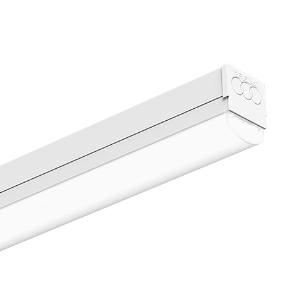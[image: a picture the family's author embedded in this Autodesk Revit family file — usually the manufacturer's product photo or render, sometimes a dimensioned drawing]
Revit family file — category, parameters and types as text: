
# Revit family: 3f_filippi_-_3f_zeta_d_3f_filippi_-_10870_-_3f_zeta_d_1x22_led_l1489
name_source: partatom
category: Lighting Fixtures
units: mm (PartAtom-declared; Revit-internal decimal feet)

## family parameters
Cut with Voids When Loaded = No
Host = Face
Light Source = No
Part Type = Normal
Room Calculation Point = No
Round Connector Dimension = Use Diameter
Shared = No

## types (1)
- 3F Filippi - 3F Zeta D (1 x LED, 3118 lm, 24.5 W, 4000 K)
    Apparent Load = 25 VA
    Approval mark = CE
    CIE Flux Codes = 42 71 90 91 100
    Color Rendering = 80
    Color Temperature = 4000 K
    Control Gear = Electronic ballast
    Default Elevation = 1800 mm
    Description = ILLUMINOTECHNICAL
Luminous efficiency 100% (DLOR 91%, ULOR 9%).
Initial luminous flux of the luminaire 3118 lm.
Diffused symmetric distribution.
Installation Interdistance Transv.D = 1.31 x hu - Long.D = 1.25 x hu.
Tabular UGR (CIE 117 - 4H-8H; S=0.25H; 70/50/20): RUG 23.8 - 22.2.
Beam angle: 130° - 112°.
Luminous efficacy 127 lm/W.
Lifetime (L93/B10): 30000 h. (tq+25°C)
Lifetime (L90/B10): 50000 h. (tq+25°C)
Lifetime (L85/B10): 80000 h. (tq+25°C)
Lifetime (L80/B10): 100000 h. (tq+25°C)
Sudden decreased luminous flux after 50000 hours: 0% (C0).
Photobiological safety in compliance with IEC/TR 62778: RG0 risk exempt, (IEC 62471).
In compliance with IEC/EN 62722-2-1 - IEC/EN 62717 standards.

SOURCE
Linear LED module 22W/840.
Energy efficiency class (UE 2019/2020 - UE 2019/2015): D.
CIE 13.3 Colour rendering index: CRI >80 (R9 <50%).
IES TM-30 Fidelity Index: Rf = 84 Rg = 95.
CCT nominal colour temperature 4000 K.
Colour initial tolerance (MacAdam): SDCM 3.

MECHANICAL
Housing in hot-galvanised steel, painted in white polyester, obtained through rolling process.
Light unit in hot-galvanised steel, painted in white polyester base with fixing springs and retractable safety hooks in stainless steel.
Curved screen in self-extinguishing polycarbonate, UV stabilised, opal, with smooth outer surface.
End caps in white polycarbonate.
Pair of stainless steel sliding brackets with sliding block screws.
Luminaire with limited surface temperature. - D - (EN 60598-2-24)
Dimensions: 1489x62 mm, height 81 mm. Weight 3.36 kg.
IP40 protection degree.
Mechanical strength to impacts IK06 (1 joule).
Glow-wire test resistance 850°C.

ELECTRICAL
Halogen Free electronic wiring 230V-50/60Hz, power factor 0.90, THD <25%, constant output current, SELV, class I, 1 driver.
Power of the luminaire 24.5 W.
ENEC - CE.
SAFE FLICKER: PstLM=<1 and SVM=<0.4 (IEC TR 61547-1 and IEC TR 63158), to ensure a more comfortable and safe light.
Luminaire compliant with EN 60598-2-22 for power supply from a centralised emergency system CPSS (Central Power Supply System), not incorporated in the luminaire - high risk areas excluded. The default power and flux are 100% in AC and 100% in DC.
Ambient temperature from 0°C to +25°C.
Temperature class T6 max 85°C.
Relative humidity UR: <85%.

INSTALLATION
Ceiling / Suspended / Wall.
All accessories dedicated to this product are available on the Catalog and on our website www.3F-Filippi.com.

APPLICATIONS
Suitable product for food production plants (HACCP), IFS (Food Version 6), BRC (GSFS Food Version 7).
In commercial environments, exhibition areas, shops and stores.

WARNING
Luminaire designed for disposal/recycling at end-of-life.
Replaceable (LED only) light source by a professional. Replaceable control gear by a professional.
    Height = 81 mm
    Lamp = 1 x LED
    Lamp Light Flux = 3118 lm
    Lamp Power = 24.5 W
    Lamp count = 1
    Length = 1489 mm
    Lifetime = 50000 h
    Luminous efficacy = 127 lm/W
    Manufacturer = 3F Filippi
    ModVariant = No
    Model = 3F Filippi - 10870 - 3F Zeta D 1x22 LED L1489
    Mounting Place = Ceiling
    Mounting Type = Pendant
    Number of Poles = 1
    OnlyDefault = Yes
    Power Factor = 1
    Product Name = 3F Filippi - 3F Zeta D
    Product group = pendant luminaire
    ProductGroupID = 9
    Protection Class = Protection class I
    Protection Degree = IP 40
    RLX_Detail_Level = 1
    RLX_Emergency_Light_Flux = 0 lm
    RLX_Emergency_Type = 0
    RLX_Emergency_Type_DB = No
    RlxData = <blob elided: 33337 chars, md5=28099d96>
    Socket = socket
    Standby Power = 0 W
    System Light Flux = 3118 lm
    System Power = 25 W
    Type Comments = Product without accessories
    Type Image = 3ffilippi_3f_zeta_d.jpg
    URL = http://relux.com
    VarID = ---
    Voltage = 0 V
    Weight = 0.00 kg
    Width = 62 mm  [stored 0.203412 ft]

note: [stored X ft] marks values corroborated as IEEE doubles in the binary element streams (Revit-internal decimal feet)

## geometry (parser evidence)
native form markers: Blend x4, Sweep x11
no freeform markers — native parametric forms only
